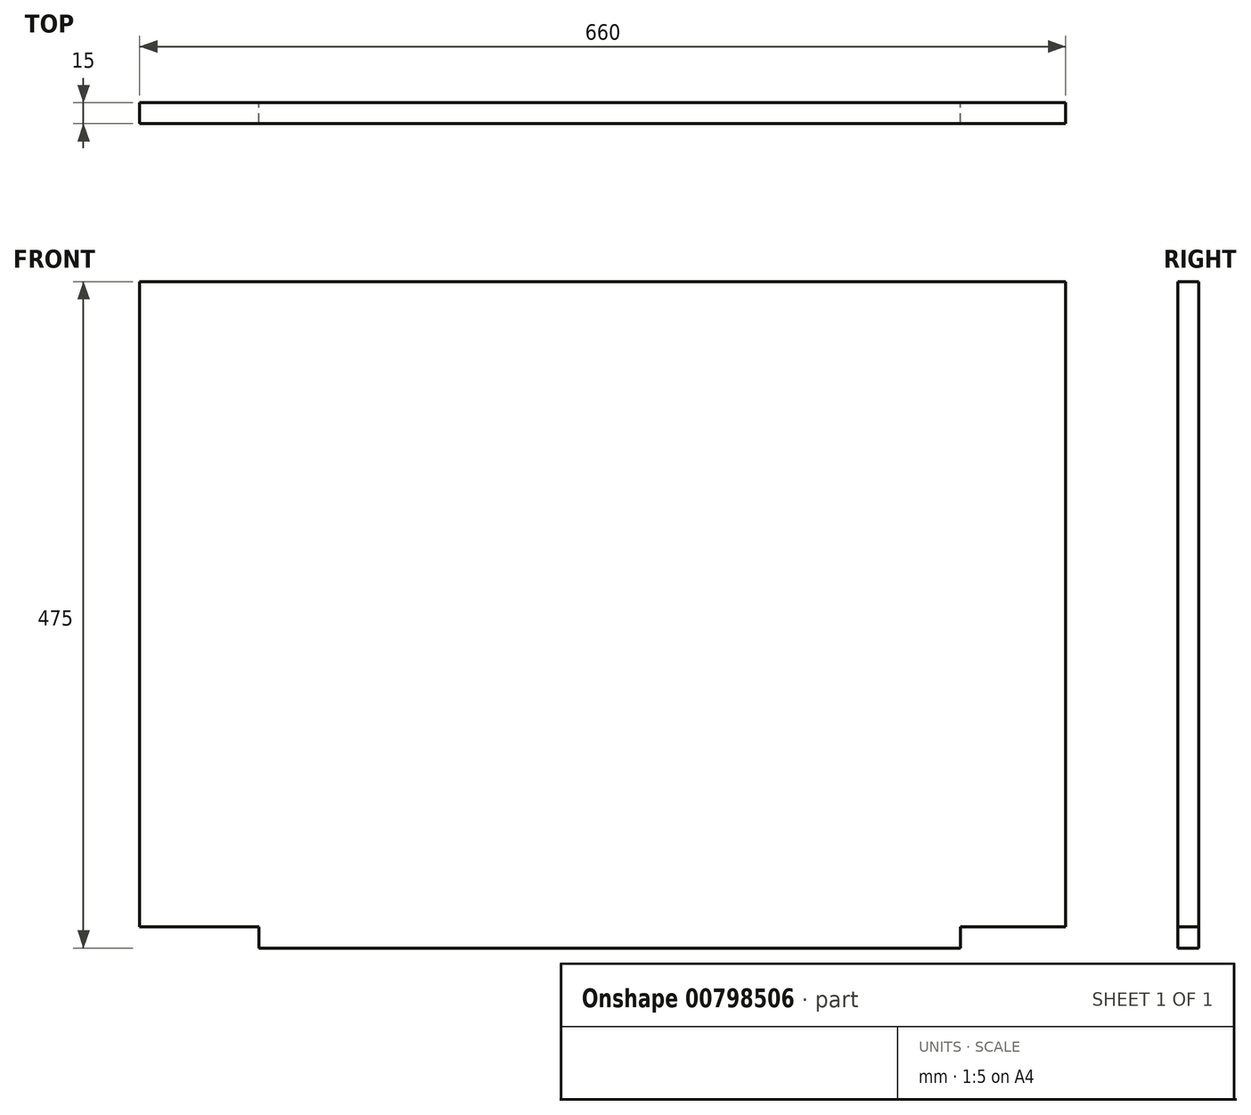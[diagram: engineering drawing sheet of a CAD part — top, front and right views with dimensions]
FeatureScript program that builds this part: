
annotation { "Feature Type Name" : "Feature", "Feature Type Description" : "" }
export const myFeature = defineFeature(function(context is Context, id is Id, definition is map)
    precondition{}
    {
        {
            var Q0;
            Q0=qCreatedBy(makeId("Front.planeOp"),FACE);
            var sketch = newSketch(context, id + "F0", { "sketchPlane" : qUnion([Q0])});
            skLineSegment(sketch, "E0.bottom", {"start": v(0, 0) * mm, "end": v(660, 0) * mm});
            skLineSegment(sketch, "E0.top", {"start": v(0, -460) * mm, "end": v(660, -460) * mm});
            skLineSegment(sketch, "E0.left", {"start": v(0, 0) * mm, "end": v(0, -460) * mm});
            skLineSegment(sketch, "E0.right", {"start": v(660, 0) * mm, "end": v(660, -460) * mm});
            skLineSegment(sketch, "E1.bottom", {"start": v(85, -460) * mm, "end": v(585, -460) * mm});
            skLineSegment(sketch, "E1.top", {"start": v(85, -475) * mm, "end": v(585, -475) * mm});
            skLineSegment(sketch, "E1.left", {"start": v(85, -460) * mm, "end": v(85, -475) * mm});
            skLineSegment(sketch, "E1.right", {"start": v(585, -460) * mm, "end": v(585, -475) * mm});
            skSolve(sketch);
        }
        {
            var Q0;
            Q0=makeQuery(id+"F0.imprint","IMPRINT",FACE,{"disambiguationData":[TD([[makeQuery(id+"F0.imprint","IMPRINT",EDGE,{"derivedFrom":sQuery(id+"F0.wireOp",EDGE,"E0.bottom")}),-1.0]])]});
            var Q1;
            Q1=makeQuery(id+"F0.imprint","IMPRINT",FACE,{"disambiguationData":[TD([[makeQuery(id+"F0.imprint","IMPRINT",EDGE,{"derivedFrom":sQuery(id+"F0.wireOp",EDGE,"E1.top")}),1.0]])]});
            extrude(context, id + "F1", {"entities" : qUnion([Q0, Q1]), "depth" : 15 * mm, "offsetDistance" : 25 * mm});
        }
    });
